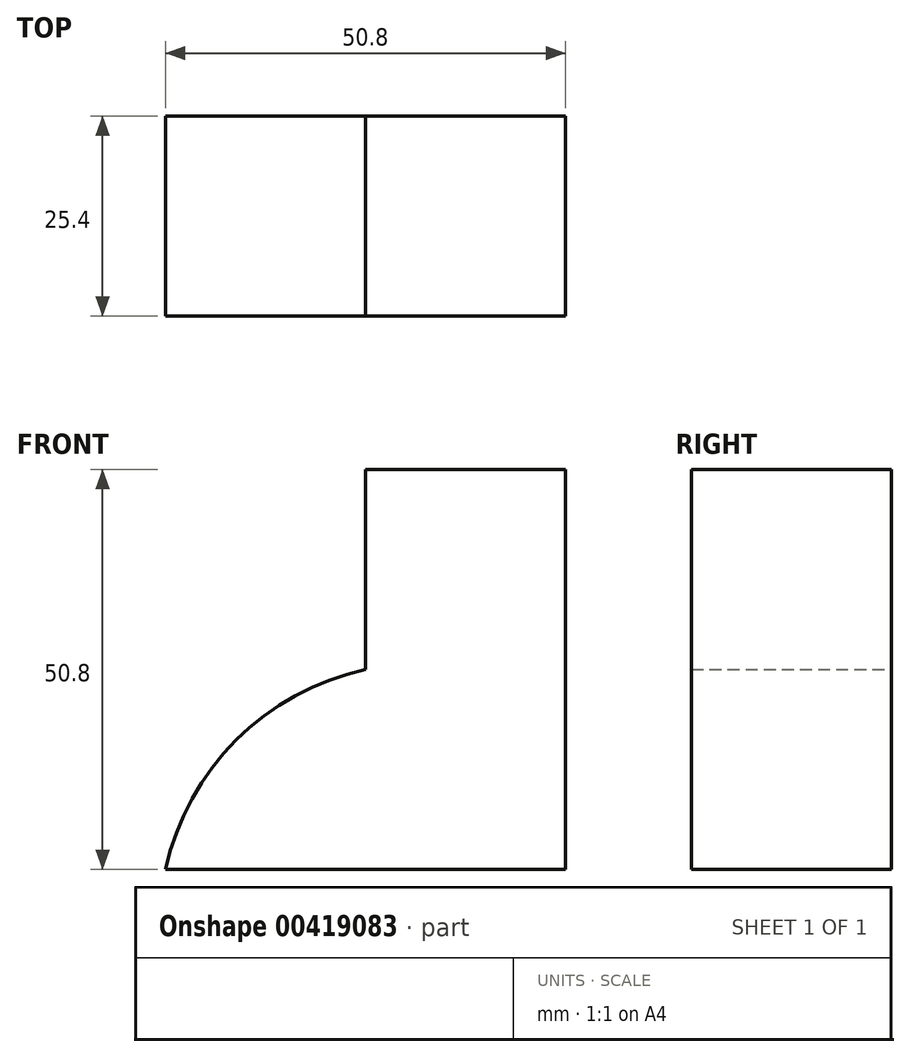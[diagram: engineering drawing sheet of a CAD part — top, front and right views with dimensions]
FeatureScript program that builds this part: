
annotation { "Feature Type Name" : "Feature", "Feature Type Description" : "" }
export const myFeature = defineFeature(function(context is Context, id is Id, definition is map)
    precondition{}
    {
        {
            var Q0;
            Q0=qCreatedBy(makeId("Front.planeOp"),FACE);
            var sketch = newSketch(context, id + "F0", { "sketchPlane" : qUnion([Q0])});
            skLineSegment(sketch, "E0", {"start": v(0, 0) * mm, "end": v(50.8, 0) * mm});
            skLineSegment(sketch, "E1", {"start": v(50.8, 0) * mm, "end": v(50.8, 50.8) * mm});
            skLineSegment(sketch, "E2", {"start": v(50.8, 50.8) * mm, "end": v(25.4, 50.8) * mm});
            skLineSegment(sketch, "E3", {"start": v(25.4, 50.8) * mm, "end": v(25.4, 25.4) * mm});
            skArc(sketch, "E4", {"start": v(25.4, 25.4) * mm, "mid": v(8.97, 16.43) * mm, "end": v(0, 0) * mm});
            skSolve(sketch);
        }
        {
            var Q0;
            Q0=makeQuery(id+"F0.imprint","IMPRINT",FACE,{"disambiguationData":[TD([[makeQuery(id+"F0.imprint","IMPRINT",EDGE,{"derivedFrom":sQuery(id+"F0.wireOp",EDGE,"E0")}),1.0]])]});
            extrude(context, id + "F1", {"entities" : qUnion([Q0]), "depth" : 25.4 * mm});
        }
    });
